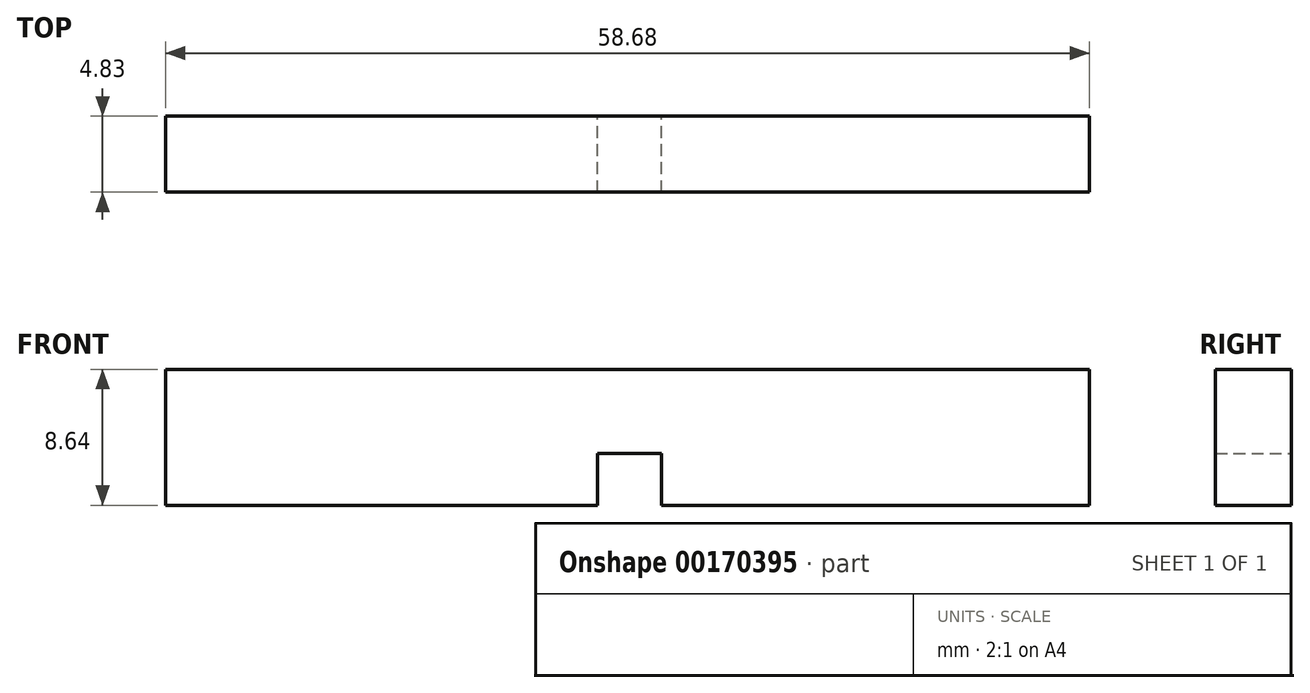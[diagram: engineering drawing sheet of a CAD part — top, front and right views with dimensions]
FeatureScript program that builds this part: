
annotation { "Feature Type Name" : "Feature", "Feature Type Description" : "" }
export const myFeature = defineFeature(function(context is Context, id is Id, definition is map)
    precondition{}
    {
        {
            var Q0;
            Q0=qCreatedBy(makeId("Front.planeOp"),FACE);
            var sketch = newSketch(context, id + "F0", { "sketchPlane" : qUnion([Q0])});
            skLineSegment(sketch, "E0.bottom", {"start": v(-29.34, 4.32) * mm, "end": v(29.34, 4.32) * mm});
            skLineSegment(sketch, "E0.top", {"start": v(-29.34, -4.32) * mm, "end": v(-1.9, -4.32) * mm});
            skLineSegment(sketch, "E0.left", {"start": v(-29.34, 4.32) * mm, "end": v(-29.34, -4.32) * mm});
            skLineSegment(sketch, "E0.right", {"start": v(29.34, 4.32) * mm, "end": v(29.34, -4.32) * mm});
            skLineSegment(sketch, "E1.bottom", {"start": v(-1.9, -1.02) * mm, "end": v(2.16, -1.02) * mm});
            skLineSegment(sketch, "E1.left", {"start": v(-1.9, -1.02) * mm, "end": v(-1.9, -4.32) * mm});
            skLineSegment(sketch, "E1.right", {"start": v(2.16, -1.02) * mm, "end": v(2.16, -4.32) * mm});
            skLineSegment(sketch, "E2.trimOffspring", {"start": v(2.16, -4.32) * mm, "end": v(29.34, -4.32) * mm});
            skSolve(sketch);
        }
        {
            var Q0;
            Q0=makeQuery(id+"F0.imprint","IMPRINT",FACE,{"disambiguationData":[TD([[makeQuery(id+"F0.imprint","IMPRINT",EDGE,{"derivedFrom":sQuery(id+"F0.wireOp",EDGE,"E0.bottom")}),-1.0]])]});
            extrude(context, id + "F1", {"entities" : qUnion([Q0]), "depth" : 4.83 * mm});
        }
    });
